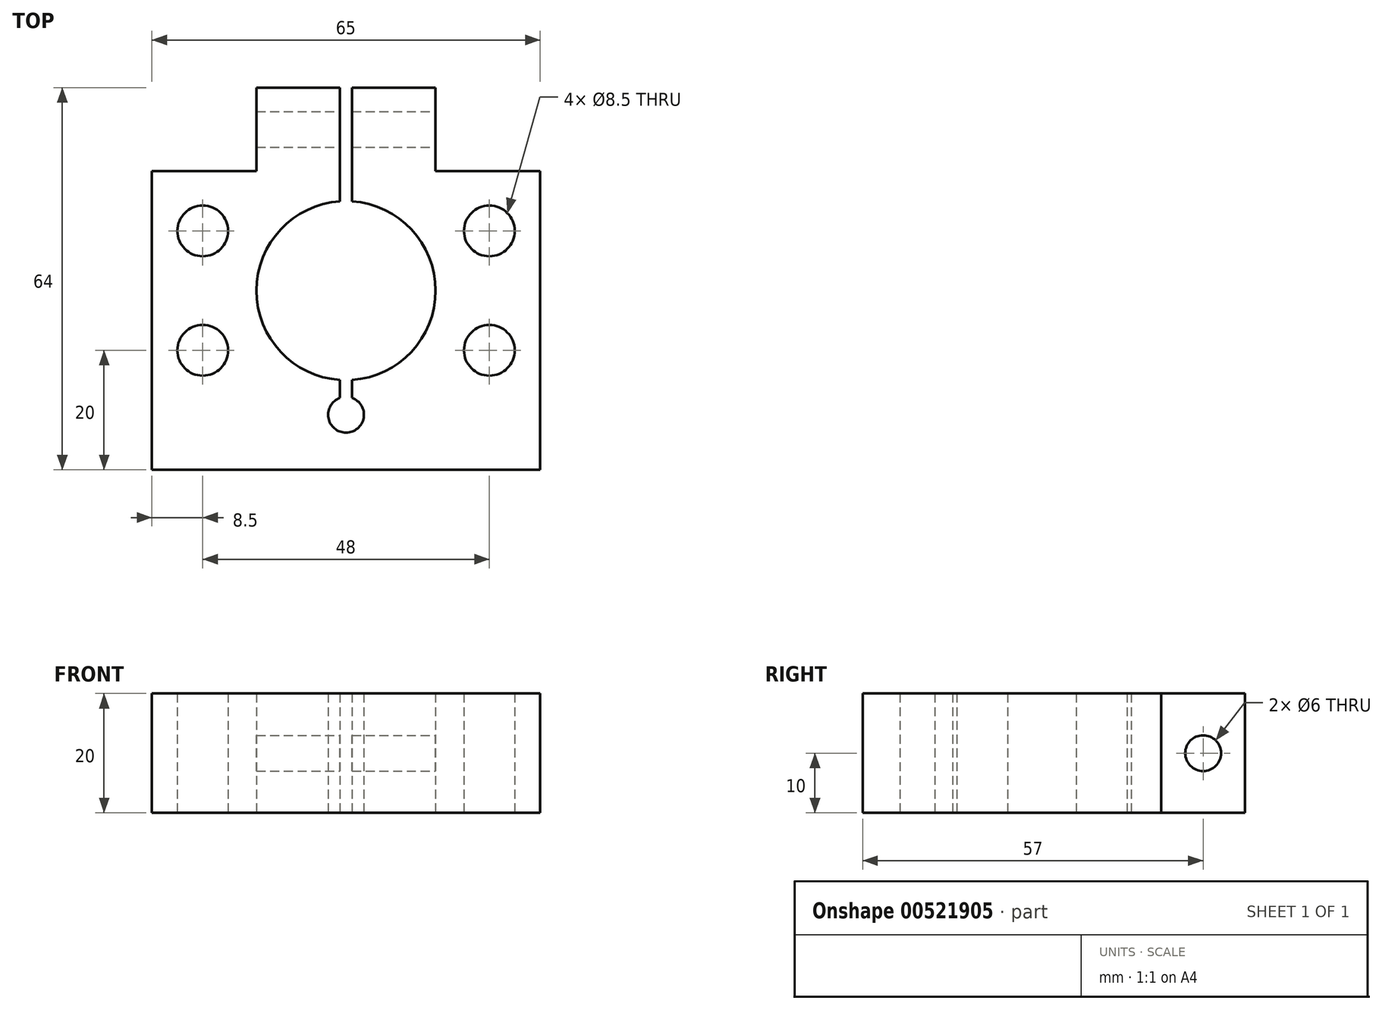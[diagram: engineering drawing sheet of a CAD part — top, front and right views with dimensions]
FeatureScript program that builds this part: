
annotation { "Feature Type Name" : "Feature", "Feature Type Description" : "" }
export const myFeature = defineFeature(function(context is Context, id is Id, definition is map)
    precondition{}
    {
        {
            var Q0;
            Q0=qCreatedBy(makeId("Top.planeOp"),FACE);
            var sketch = newSketch(context, id + "F0", { "sketchPlane" : qUnion([Q0])});
            skLineSegment(sketch, "E0.bottom", {"start": v(-15, 34) * mm, "end": v(-1, 34) * mm});
            skLineSegment(sketch, "E0.top", {"start": v(-32.5, -30) * mm, "end": v(32.5, -30) * mm});
            skLineSegment(sketch, "E0.left", {"start": v(-32.5, 20) * mm, "end": v(-32.5, -30) * mm});
            skLineSegment(sketch, "E0.right", {"start": v(32.5, 20) * mm, "end": v(32.5, -30) * mm});
            skArc(sketch, "E1", {"start": v(-1, 14.97) * mm, "mid": v(-15, 0) * mm, "end": v(-1, -14.97) * mm});
            skArc(sketch, "E2", {"start": v(-1, -17.97) * mm, "mid": v(0, -23.8) * mm, "end": v(1, -17.97) * mm});
            skLineSegment(sketch, "E3", {"start": v(-1, 34) * mm, "end": v(-1, 14.97) * mm});
            skLineSegment(sketch, "E4", {"start": v(1, 34) * mm, "end": v(1, 14.97) * mm});
            skLineSegment(sketch, "E5", {"start": v(0, 15) * mm, "end": v(0, 0) * mm, "construction": true});
            skLineSegment(sketch, "E6.trimOffspring", {"start": v(1, 34) * mm, "end": v(15, 34) * mm});
            skLineSegment(sketch, "E7", {"start": v(1, -17.97) * mm, "end": v(1, -14.97) * mm});
            skLineSegment(sketch, "E8", {"start": v(-1, -17.97) * mm, "end": v(-1, -14.97) * mm});
            skArc(sketch, "E9.trimOffspring", {"start": v(1, -14.97) * mm, "mid": v(15, 0) * mm, "end": v(1, 14.97) * mm});
            skCircle(sketch, "E10", {"center": v(-24, -10) * mm, "radius": 4.25 * mm});
            skCircle(sketch, "E11", {"center": v(24, -10) * mm, "radius": 4.25 * mm});
            skCircle(sketch, "E12", {"center": v(-24, 10) * mm, "radius": 4.25 * mm});
            skLineSegment(sketch, "E13", {"start": v(-32.5, 20) * mm, "end": v(-15, 20) * mm});
            skLineSegment(sketch, "E14", {"start": v(-15, 20) * mm, "end": v(-15, 34) * mm});
            skLineSegment(sketch, "E15", {"start": v(15, 34) * mm, "end": v(15, 20) * mm});
            skLineSegment(sketch, "E16", {"start": v(15, 20) * mm, "end": v(32.5, 20) * mm});
            skCircle(sketch, "E17", {"center": v(24, 10) * mm, "radius": 4.25 * mm});
            skSolve(sketch);
        }
        {
            var Q0;
            Q0 = qSketchRegion(id + "F0", true);
            extrude(context, id + "F1", {"entities" : qUnion([Q0]), "depth" : 20 * mm, "offsetDistance" : 25 * mm});
        }
        {
            var Q0;
            Q0=makeQuery(id+"F1.opExtrude","SWEPT_FACE",FACE,{"disambiguationData":[OSD([sQuery(id+"F0.wireOp",EDGE,"E15")])]});
            var sketch = newSketch(context, id + "F2", { "sketchPlane" : qUnion([Q0])});
            skCircle(sketch, "E18", {"center": v(27, 10) * mm, "radius": 3 * mm});
            skPoint(sketch, "E18.centerSnap0", {"position": v(27, 20) * mm});
            skPoint(sketch, "E18.centerSnap1", {"position": v(20, 10) * mm});
            skSolve(sketch);
        }
        {
            var Q0;
            Q0 = qSketchRegion(id + "F2", true);
            extrude(context, id + "F3", {"entities" : qUnion([Q0]), "operationType" : NewBodyOperationType.REMOVE, "oppositeDirection" : true, "depth" : 30 * mm, "offsetDistance" : 25 * mm});
        }
    });
